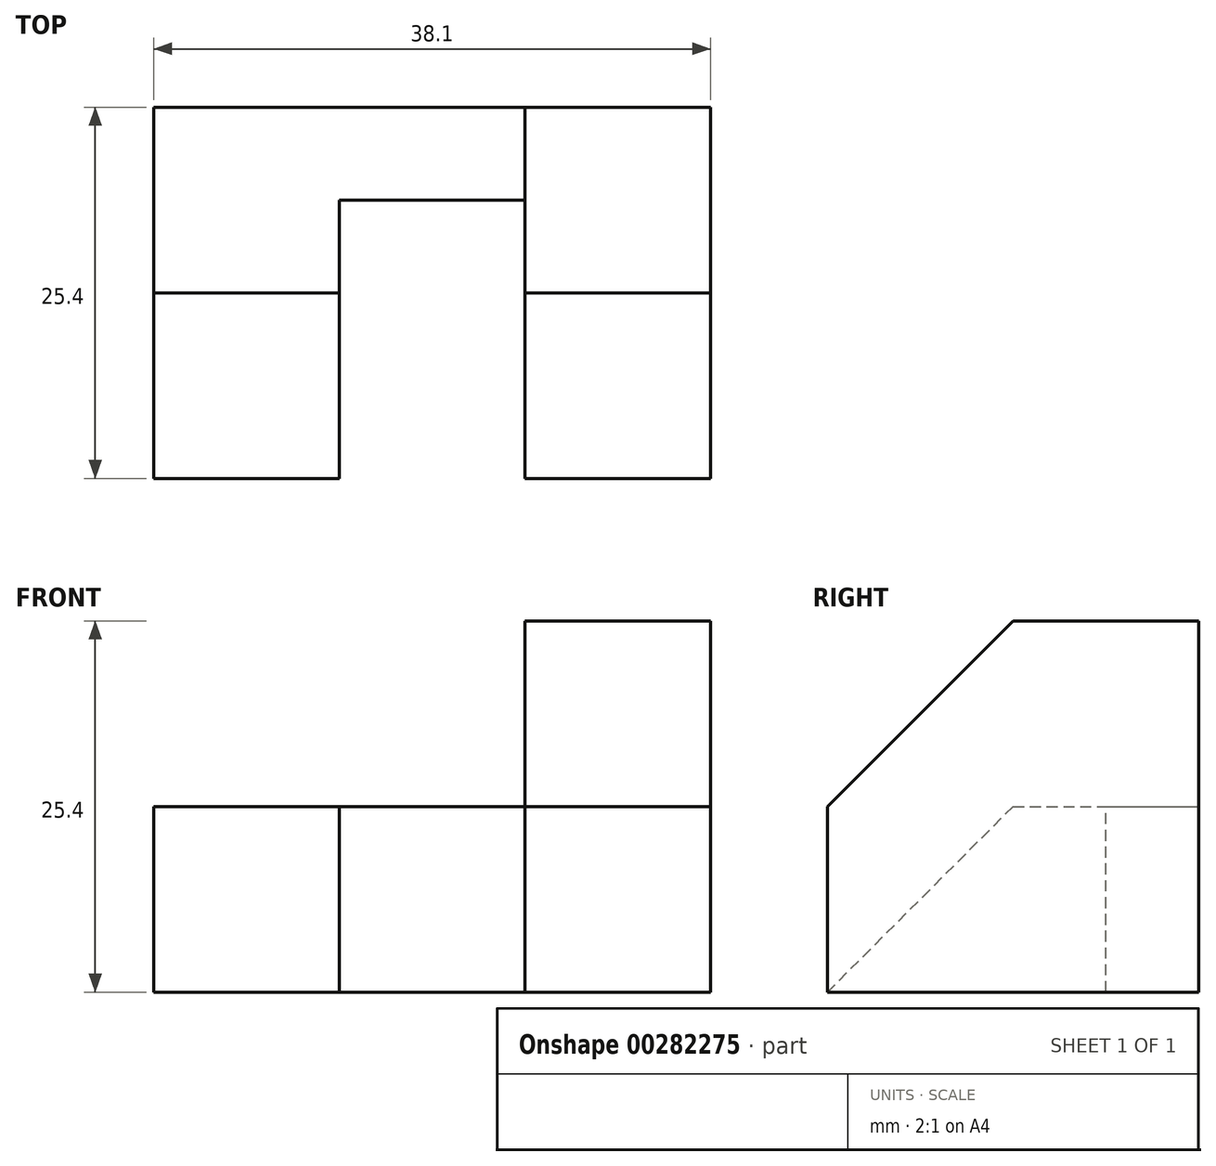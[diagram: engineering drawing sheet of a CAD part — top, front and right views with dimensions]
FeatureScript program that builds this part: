
annotation { "Feature Type Name" : "Feature", "Feature Type Description" : "" }
export const myFeature = defineFeature(function(context is Context, id is Id, definition is map)
    precondition{}
    {
        {
            var Q0;
            Q0=qCreatedBy(makeId("Right.planeOp"),FACE);
            var sketch = newSketch(context, id + "F0", { "sketchPlane" : qUnion([Q0])});
            skLineSegment(sketch, "E0", {"start": v(0, 0) * mm, "end": v(25.4, 0) * mm});
            skLineSegment(sketch, "E1", {"start": v(25.4, 0) * mm, "end": v(25.4, 25.4) * mm});
            skLineSegment(sketch, "E2", {"start": v(25.4, 25.4) * mm, "end": v(12.7, 25.4) * mm});
            skLineSegment(sketch, "E3", {"start": v(12.7, 25.4) * mm, "end": v(0, 12.7) * mm});
            skLineSegment(sketch, "E4", {"start": v(0, 12.7) * mm, "end": v(0, 0) * mm});
            skSolve(sketch);
        }
        {
            var Q0;
            Q0 = qSketchRegion(id + "F0", true);
            extrude(context, id + "F1", {"entities" : qUnion([Q0]), "depth" : 12.7 * mm});
        }
        {
            var Q0;
            Q0=makeQuery(id+"F1.opExtrude","SWEPT_FACE",FACE,{"disambiguationData":[OSD([sQuery(id+"F0.wireOp",EDGE,"E1")])]});
            var sketch = newSketch(context, id + "F2", { "sketchPlane" : qUnion([Q0])});
            skLineSegment(sketch, "E5", {"start": v(0, 0) * mm, "end": v(12.7, 0) * mm});
            skLineSegment(sketch, "E6", {"start": v(12.7, 0) * mm, "end": v(12.7, 12.7) * mm});
            skLineSegment(sketch, "E7", {"start": v(12.7, 12.7) * mm, "end": v(0, 12.7) * mm});
            skLineSegment(sketch, "E8", {"start": v(0, 12.7) * mm, "end": v(0, 0) * mm});
            skSolve(sketch);
        }
        {
            var Q0;
            Q0 = qSketchRegion(id + "F2", true);
            extrude(context, id + "F3", {"entities" : qUnion([Q0]), "operationType" : NewBodyOperationType.ADD, "oppositeDirection" : true, "depth" : 6.35 * mm});
        }
        {
            var Q0;
            Q0=makeQuery(id+"F3.boolean.opBoolean","MERGE",FACE,{"derivedFrom":[makeQuery(id+"F1.opExtrude","SWEPT_FACE",FACE,{"disambiguationData":[OSD([sQuery(id+"F0.wireOp",EDGE,"E1")])]}),makeQuery(id+"F3.opExtrude","CAP_FACE",FACE,{"disambiguationData":[OSD([sQuery(id+"F2.wireOp",EDGE,"E5"),sQuery(id+"F2.wireOp",EDGE,"E6"),sQuery(id+"F2.wireOp",EDGE,"E7"),sQuery(id+"F2.wireOp",EDGE,"E8")])],"isStart":true})]});
            var sketch = newSketch(context, id + "F4", { "sketchPlane" : qUnion([Q0])});
            skLineSegment(sketch, "E9.bottom", {"start": v(12.7, 12.7) * mm, "end": v(25.4, 12.7) * mm});
            skLineSegment(sketch, "E9.top", {"start": v(12.7, 0) * mm, "end": v(25.4, 0) * mm});
            skLineSegment(sketch, "E9.left", {"start": v(12.7, 12.7) * mm, "end": v(12.7, 0) * mm});
            skLineSegment(sketch, "E9.right", {"start": v(25.4, 12.7) * mm, "end": v(25.4, 0) * mm});
            skSolve(sketch);
        }
        {
            var Q0;
            Q0 = qSketchRegion(id + "F4", true);
            extrude(context, id + "F5", {"entities" : qUnion([Q0]), "operationType" : NewBodyOperationType.ADD, "oppositeDirection" : true, "depth" : 25.4 * mm});
        }
        {
            var Q0;
            Q0=makeQuery(id+"F5.opExtrude","SWEPT_FACE",FACE,{"disambiguationData":[OSD([sQuery(id+"F4.wireOp",EDGE,"E9.right")])]});
            var sketch = newSketch(context, id + "F6", { "sketchPlane" : qUnion([Q0])});
            skLineSegment(sketch, "E10", {"start": v(0, 0) * mm, "end": v(0, 12.7) * mm});
            skLineSegment(sketch, "E11", {"start": v(0, 12.7) * mm, "end": v(-12.7, 12.7) * mm});
            skLineSegment(sketch, "E12", {"start": v(-12.7, 12.7) * mm, "end": v(0, 0) * mm});
            skSolve(sketch);
        }
        {
            var Q0;
            Q0 = qSketchRegion(id + "F6", true);
            extrude(context, id + "F7", {"entities" : qUnion([Q0]), "operationType" : NewBodyOperationType.REMOVE, "oppositeDirection" : true, "depth" : 12.7 * mm});
        }
    });
